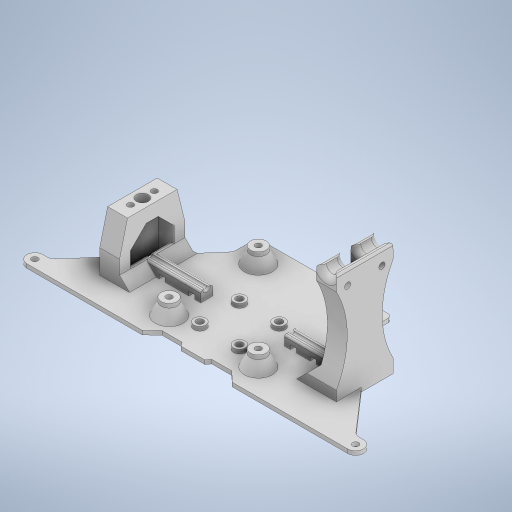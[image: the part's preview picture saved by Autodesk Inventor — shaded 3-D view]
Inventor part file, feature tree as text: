
AUTODESK INVENTOR PART (.ipt)
format: ipt  version: 2023 (Build 270158000, 158)  size: 791,040 bytes
history: native  units: in
note: dims shown in document units (in); Inventor stores cm internally (conversion verified against a paired STEP export)
features: sketch x24, extrude x23, chamfer x5, fillet x4, other x1
ambient origin geometry x8: Origin, YZ Plane, XZ Plane, XY Plane, X Axis, Y Axis, Z Axis, Center Point
bodies: Solid1 (feature_tree)
feature tree (57):
  extrude  "Extrusion1"  Depth=0.315in
  extrude  "Extrusion2"  Depth=0.315in
  extrude  "Extrusion3"  Depth=0.315in
  extrude  "Extrusion4"  Depth=0.0787in TaperAngle=0.0deg
  extrude  "Extrusion5"  Depth=0.315in
  extrude  "Extrusion6"  Depth=0.315in
  extrude  "Extrusion15"  Depth=0.315in
  sketch  "Sketch16"  dims[d27=1.7717in]
  chamfer  "Chamfer2"  Distance=0.315in
  extrude  "Extrusion17"  Depth=0.1575in
  extrude  "Extrusion18"  Depth=0.2362in
  extrude  "Extrusion24"  Depth=0.2362in
  sketch  "Sketch27"  dims[d30=1.7717in]
  extrude  "Extrusion29"  Depth=0.0787in TaperAngle=0.0deg
  extrude  "Extrusion30"  Depth=1.1811in
  extrude  "Extrusion31"  Depth=0.7874in
  extrude  "Extrusion32"  Depth=0.0787in TaperAngle=0.0deg
  fillet  "Fillet3"  Radius=0.0787in
  extrude  "Extrusion33"  Depth=0.0787in TaperAngle=0.0deg
  fillet  "Fillet4"  Radius=0.9843in
  chamfer  "Chamfer5"  Distance=0.1378in
  extrude  "Extrusion34"  Depth=0.1181in TaperAngle=0.0deg
  fillet  "Fillet5"  Radius=0.2402in
  extrude  "Extrusion35"  Depth=0.0787in
  extrude  "Extrusion36"  Depth=0.2362in
  extrude  "Extrusion37"  Depth=0.2362in
  extrude  "Extrusion38"  Depth=0.0787in
  extrude  "Extrusion39"  Depth=0.0787in
  extrude  "Extrusion40"  Depth=0.1181in TaperAngle=45.0deg
  fillet  "Fillet6"  Radius=0.1969in
  chamfer  "Chamfer6"  Distance=0.1969in
  chamfer  "Chamfer7"  Distance=0.0787in
  chamfer  "Chamfer8"  Distance=0.0787in
  extrude  "Extrusion41"  Depth=0.1181in
  sketch  "Sketch1"  dims[d0=0.0984in d1=0.0984in d2=0.1181in d3=0.1181in d4=0.315in]
  sketch  "Sketch2"  dims[d5=0.315in d6=0.315in]
  sketch  "Sketch3"  dims[d7=0.315in d8=2.3622in]
  sketch  "Sketch4"  dims[d18=0.1575in d19=0.0787in d20=0.0in]
  sketch  "Sketch5"  dims[d21=2.3622in d22=0.315in]
  sketch  "Sketch6"  dims[d23=0.315in d24=0.315in]
  sketch  "Sketch15"  dims[d25=0.315in d26=1.7717in]
  sketch  "Sketch17"  dims[d28=1.7717in]
  sketch  "Sketch22"  dims[d29=0.2756in]
  other  "Image1"
  sketch  "Sketch28"  dims[d31=0.2953in d36=0.315in d37=0.0in]
  sketch  "Sketch29"  dims[d38=0.1575in d39=0.0in d40=0.7874in]
  sketch  "Sketch30"  dims[d41=0.7874in d42=0.2362in]
  sketch  "Sketch31"  dims[d43=0.2362in d44=0.2362in]
  sketch  "Sketch32"  dims[d45=0.2362in d46=0.0787in d47=0.0in]
  sketch  "Sketch33"  dims[d49=0.9843in d50=1.1811in]
  sketch  "Sketch34"  dims[d51=2.3622in d52=0.7874in]
  sketch  "Sketch35"  dims[d53=0.9843in d54=0.0787in d55=0.0in d56=0.0787in d57=0.0in]
  sketch  "Sketch36"  dims[d61=0.0787in d62=0.0in d63=0.0787in d64=0.0in d65=0.9843in]
  sketch  "Sketch37"  dims[d66=1.1811in]
  sketch  "Sketch38"  dims[d108=0.1378in]
  sketch  "Sketch39"  dims[d109=0.1378in]
  sketch  "Sketch40"  dims[d110=0.1378in d111=0.1378in d112=0.1181in d113=0.0in d114=0.2402in d115=0.1378in d116=0.2362in d117=0.2362in d118=1.6614in d119=0.2402in d122=0.1181in d123=0.2362in d124=45.0deg d125=0.1969in d126=0.1969in d127=0.0787in d128=0.0in d129=0.0787in d130=0.0in d168=0.1181in d169=0.1181in d170=0.1181in d171=0.1181in d172=0.1969in d173=0.0in d204=1.1024in d205=1.1024in d206=0.1575in d207=0.1575in d209=1.1024in d216=0.3937in d217=2.6575in d218=0.3937in d219=2.6575in d220=0.1575in d221=0.1693in d222=0.1181in d223=1.3189in d224=0.2362in d225=1.1024in d226=0.0315in d227=0.1181in d228=1.3189in d229=0.2362in d230=0.2362in d231=0.2362in d232=0.1969in d233=0.0in d234=0.3937in d235=1.126in d236=2.1654in d237=0.0in d238=0.2362in d239=0.0in d240=0.0in d241=0.2362in d242=1.9685in d243=0.2953in d244=0.0in d245=0.1181in d246=0.4724in d247=0.6811in d248=0.1181in d249=0.1181in d250=0.1969in d251=0.2953in d252=0.0in d253=0.0394in d254=1.7717in d255=1.7717in d256=0.3937in d257=0.0787in d258=45.0deg d259=0.0787in d260=0.3937in d261=0.0in d262=0.0394in d263=0.1181in d264=0.3937in d265=0.1181in d266=0.0787in d267=0.1181in d268=0.0787in d269=0.3937in d270=0.0in d272=0.5315in d273=0.5315in d274=1.1024in d275=0.0in d276=0.2362in d277=1.1024in d278=0.0in d279=0.315in d280=0.8661in d281=0.6299in d282=0.315in d283=0.0in d285=0.3937in d286=0.0in d287=0.2362in d288=0.8661in d289=0.1181in d290=0.5906in d291=0.1181in d292=0.0787in d293=0.1181in d294=0.0787in d295=0.0in d296=0.0787in d297=0.3937in d298=0.0in d299=0.0394in d300=0.1575in d301=0.6299in d302=45.0deg d303=0.1575in d304=0.6299in d305=45.0deg d306=0.2362in d307=0.2362in d308=0.1181in d309=0.1181in d310=0.1969in d311=0.6299in d312=45.0deg d313=0.315in d314=0.0787in d316=0.315in d317=0.315in d318=0.315in d319=0.315in d320=0.0787in d321=0.0in d142=0.0in d143=0.0in d144=0.0in d145=0.0in d182=0.0197in d183=0.0344in d184=0.0197in d185=0.0344in d215=0.0197in]
